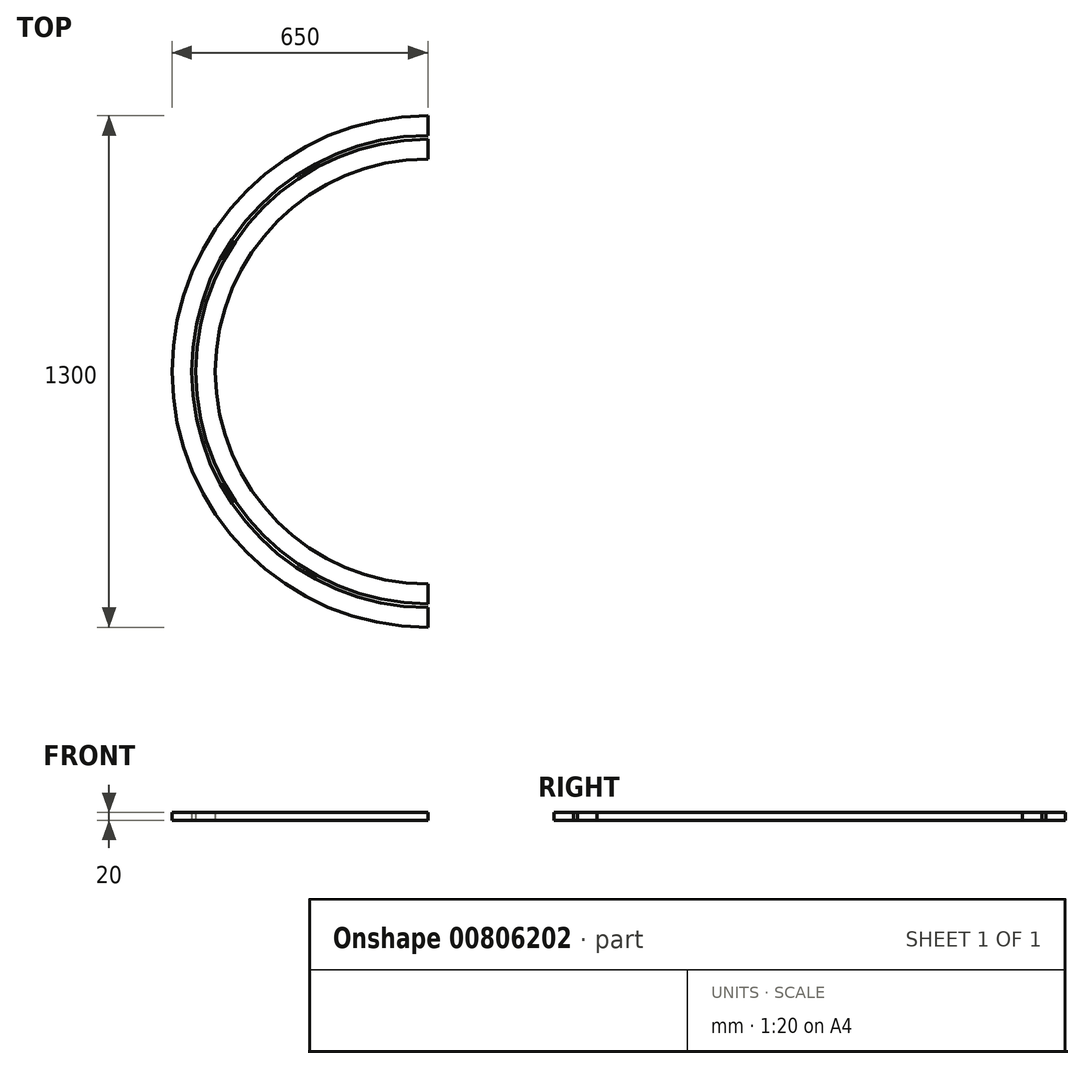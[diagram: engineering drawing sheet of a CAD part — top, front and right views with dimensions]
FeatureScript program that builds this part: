
annotation { "Feature Type Name" : "Feature", "Feature Type Description" : "" }
export const myFeature = defineFeature(function(context is Context, id is Id, definition is map)
    precondition{}
    {
        {
            var Q0;
            Q0=qCreatedBy(makeId("Top.planeOp"),FACE);
            var sketch = newSketch(context, id + "F0", { "sketchPlane" : qUnion([Q0])});
            skArc(sketch, "E0", {"start": v(0, 600) * mm, "mid": v(-600, 0) * mm, "end": v(0, -600) * mm});
            skArc(sketch, "E1", {"start": v(0, 650) * mm, "mid": v(-650, 0) * mm, "end": v(0, -650) * mm});
            skLineSegment(sketch, "E2", {"start": v(0, 540) * mm, "end": v(0, 590) * mm});
            skLineSegment(sketch, "E3", {"start": v(0, -540) * mm, "end": v(0, -590) * mm});
            skArc(sketch, "E4", {"start": v(0, 590) * mm, "mid": v(-590, 0) * mm, "end": v(0, -590) * mm});
            skArc(sketch, "E5", {"start": v(0, 540) * mm, "mid": v(-540, 0) * mm, "end": v(0, -540) * mm});
            skLineSegment(sketch, "E6.trimOffspring", {"start": v(0, 600) * mm, "end": v(0, 650) * mm});
            skLineSegment(sketch, "E7.trimOffspring", {"start": v(0, -600) * mm, "end": v(0, -650) * mm});
            skSolve(sketch);
        }
        {
            var Q0;
            Q0=qSketchRegion(id+"F0",true);
            extrude(context, id + "F1", {"entities" : qUnion([Q0]), "depth" : 20 * mm, "offsetDistance" : 25 * mm});
        }
    });
